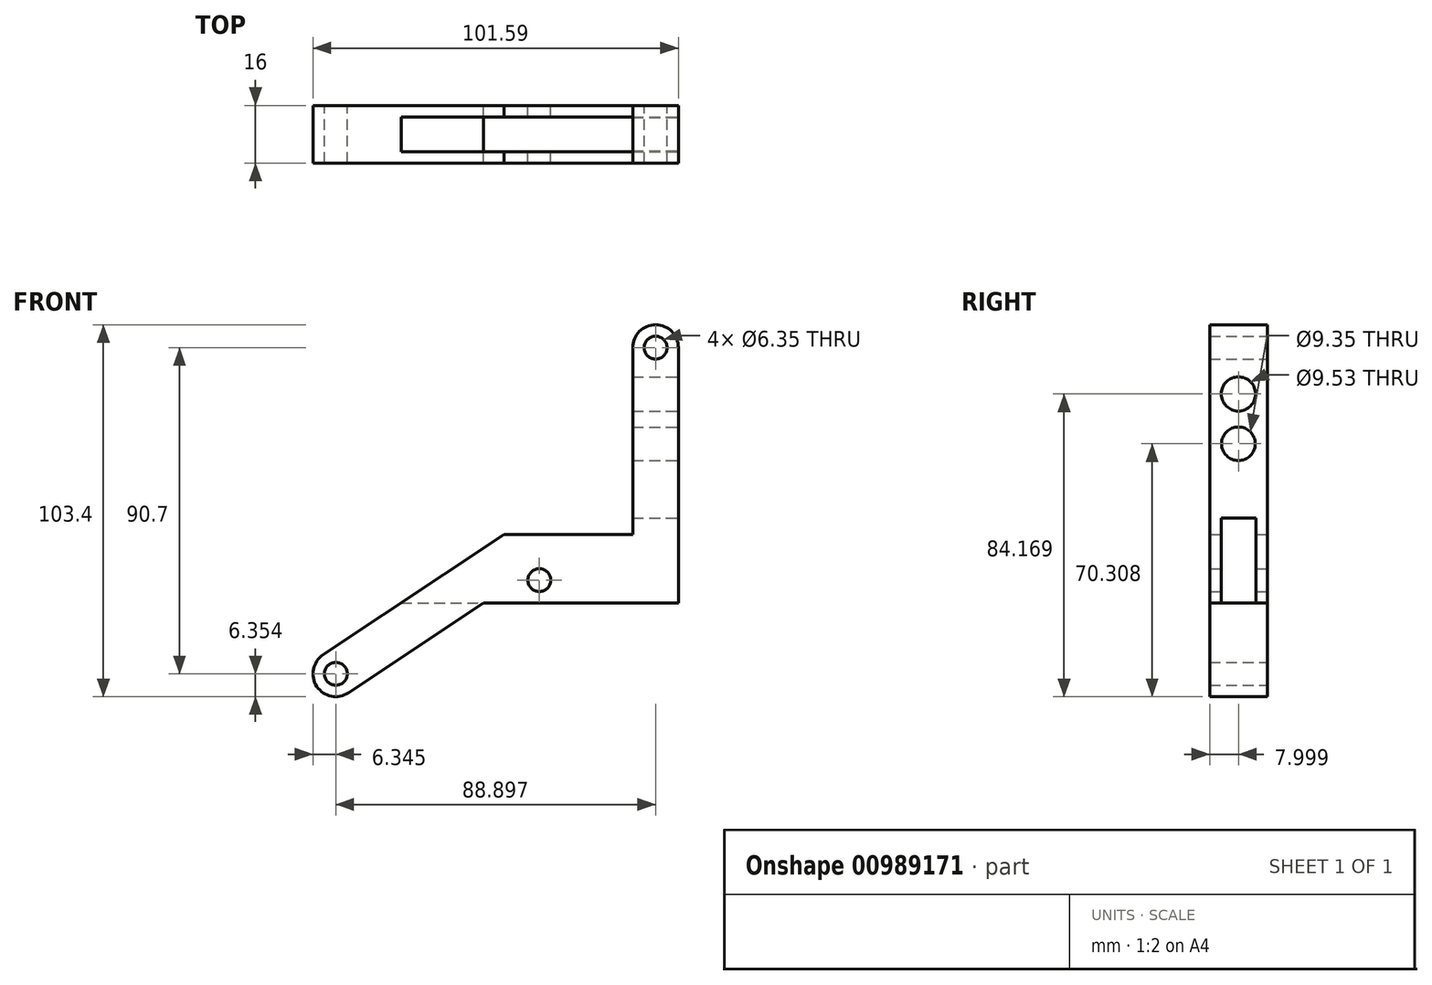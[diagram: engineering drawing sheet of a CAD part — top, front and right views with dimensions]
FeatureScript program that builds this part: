
annotation { "Feature Type Name" : "Feature", "Feature Type Description" : "" }
export const myFeature = defineFeature(function(context is Context, id is Id, definition is map)
    precondition{}
    {
        {
            var Q0;
            Q0=qCreatedBy(makeId("Front.planeOp"),FACE);
            var sketch = newSketch(context, id + "F0", { "sketchPlane" : qUnion([Q0])});
            skCircle(sketch, "E0", {"center": v(48.42, 51.56) * mm, "radius": 3.18 * mm});
            skCircle(sketch, "E1", {"center": v(16.1, -13.08) * mm, "radius": 3.18 * mm});
            skCircle(sketch, "E2", {"center": v(-40.47, -39.14) * mm, "radius": 3.18 * mm});
            skLineSegment(sketch, "E3", {"start": v(54.77, 51.56) * mm, "end": v(54.77, -19.43) * mm});
            skLineSegment(sketch, "E4", {"start": v(42.07, 51.56) * mm, "end": v(42.07, -0.38) * mm});
            skLineSegment(sketch, "E5", {"start": v(42.07, -0.38) * mm, "end": v(6.35, -0.38) * mm});
            skLineSegment(sketch, "E6", {"start": v(6.35, -0.38) * mm, "end": v(-44, -33.85) * mm});
            skLineSegment(sketch, "E7", {"start": v(-36.96, -44.42) * mm, "end": v(0.64, -19.43) * mm});
            skLineSegment(sketch, "E8", {"start": v(0.64, -19.43) * mm, "end": v(54.77, -19.43) * mm});
            skArc(sketch, "E9", {"start": v(-44, -33.85) * mm, "mid": v(-45.76, -42.65) * mm, "end": v(-36.96, -44.42) * mm});
            skArc(sketch, "E10", {"start": v(54.77, 51.56) * mm, "mid": v(48.42, 57.91) * mm, "end": v(42.07, 51.56) * mm});
            skSolve(sketch);
        }
        {
            var Q0;
            Q0=makeQuery(id+"F0.imprint","IMPRINT",FACE,{"disambiguationData":[TD([[makeQuery(id+"F0.imprint","IMPRINT",EDGE,{"derivedFrom":sQuery(id+"F0.wireOp",EDGE,"E0")}),-1.0]])]});
            extrude(context, id + "F1", {"entities" : qUnion([Q0]), "depth" : 16 * mm, "offsetDistance" : 25.4 * mm});
        }
        {
            var Q0;
            Q0=makeQuery(id+"F1.opExtrude","SWEPT_FACE",FACE,{"disambiguationData":[OSD([sQuery(id+"F0.wireOp",EDGE,"E3")])]});
            var sketch = newSketch(context, id + "F2", { "sketchPlane" : qUnion([Q0])});
            skCircle(sketch, "E11", {"center": v(-8, 38.68) * mm, "radius": 4.76 * mm});
            skCircle(sketch, "E12", {"center": v(-8, 24.82) * mm, "radius": 4.68 * mm});
            skLineSegment(sketch, "E13", {"start": v(-8, 51.56) * mm, "end": v(-8, -19.43) * mm, "construction": true});
            skLineSegment(sketch, "E14.bottom", {"start": v(-12.83, 4.23) * mm, "end": v(-3.18, 4.23) * mm});
            skLineSegment(sketch, "E14.top", {"start": v(-12.83, -19.43) * mm, "end": v(-3.18, -19.43) * mm});
            skLineSegment(sketch, "E14.left", {"start": v(-12.83, 4.23) * mm, "end": v(-12.83, -19.43) * mm});
            skLineSegment(sketch, "E14.right", {"start": v(-3.18, 4.23) * mm, "end": v(-3.18, -19.43) * mm});
            skLineSegment(sketch, "E15.bottom", {"start": v(-12.83, -19.43) * mm, "end": v(-3.16, -19.43) * mm});
            skSolve(sketch);
        }
        {
            var Q0;
            Q0 = qSketchRegion(id + "F2", true);
            extrude(context, id + "F3", {"entities" : qUnion([Q0]), "operationType" : NewBodyOperationType.REMOVE, "oppositeDirection" : true, "depth" : 119.89 * mm, "offsetDistance" : 25.4 * mm});
        }
    });
